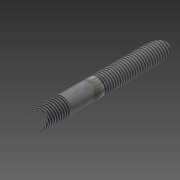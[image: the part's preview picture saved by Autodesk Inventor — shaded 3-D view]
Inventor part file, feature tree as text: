
AUTODESK INVENTOR PART (.ipt)
format: ipt  version: 2015 (Build 190159000, 159)  size: 95,744 bytes
history: native  units: mm
features: thread x2, other x1, extrude x1, sketch x1
ambient origin geometry x8: Origin, YZ Plane, XZ Plane, XY Plane, X Axis, Y Axis, Z Axis, Center Point
bodies: Body1 (feature_tree)
feature tree (5):
  other  "Bryła1"
  extrude  "Wyciągnięcie proste1"  Depth=12.0mm
  thread  "Gwint1"
  thread  "Gwint2"
  sketch  "Szkic1"
